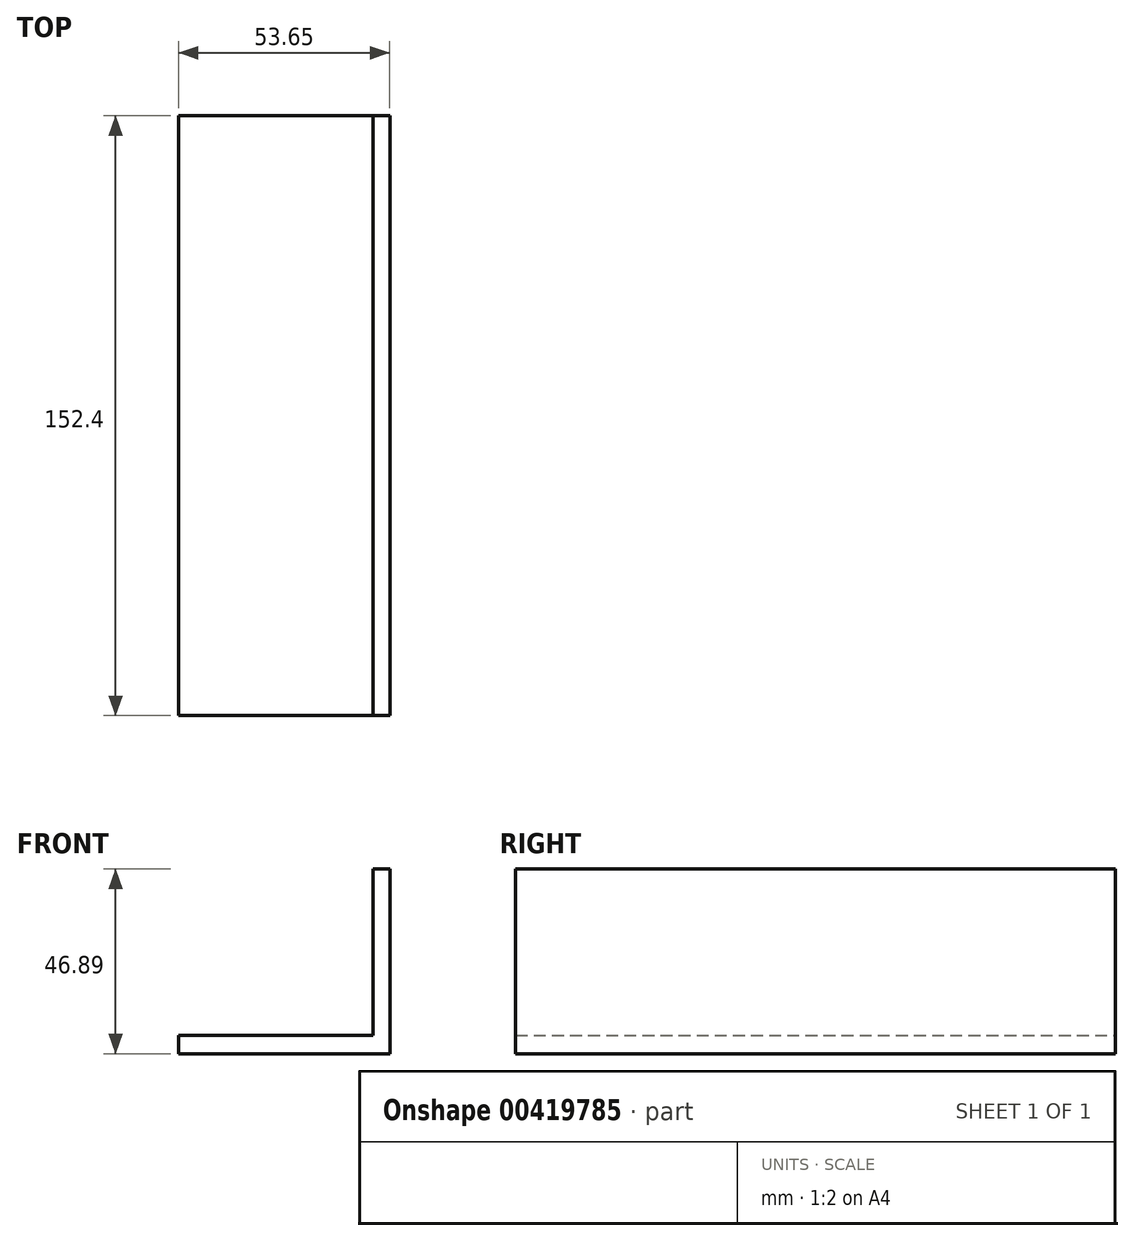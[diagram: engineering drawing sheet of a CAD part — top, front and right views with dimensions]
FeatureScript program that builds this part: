
annotation { "Feature Type Name" : "Feature", "Feature Type Description" : "" }
export const myFeature = defineFeature(function(context is Context, id is Id, definition is map)
    precondition{}
    {
        {
            var Q0;
            Q0=qCreatedBy(makeId("Front.planeOp"),FACE);
            var sketch = newSketch(context, id + "F0", { "sketchPlane" : qUnion([Q0])});
            skLineSegment(sketch, "E0", {"start": v(0, 0) * mm, "end": v(53.65, 0) * mm});
            skLineSegment(sketch, "E1", {"start": v(53.65, 0) * mm, "end": v(53.65, 46.9) * mm});
            skLineSegment(sketch, "E2", {"start": v(53.65, 46.9) * mm, "end": v(49.35, 46.9) * mm});
            skLineSegment(sketch, "E3", {"start": v(49.35, 46.9) * mm, "end": v(49.35, 4.63) * mm});
            skLineSegment(sketch, "E4", {"start": v(49.35, 4.63) * mm, "end": v(0, 4.63) * mm});
            skLineSegment(sketch, "E5", {"start": v(0, 4.63) * mm, "end": v(0, 0) * mm});
            skSolve(sketch);
        }
        {
            var Q0;
            Q0=qSketchRegion(id+"F0",true);
            extrude(context, id + "F1", {"entities" : qUnion([Q0]), "depth" : 152.4 * mm});
        }
    });
